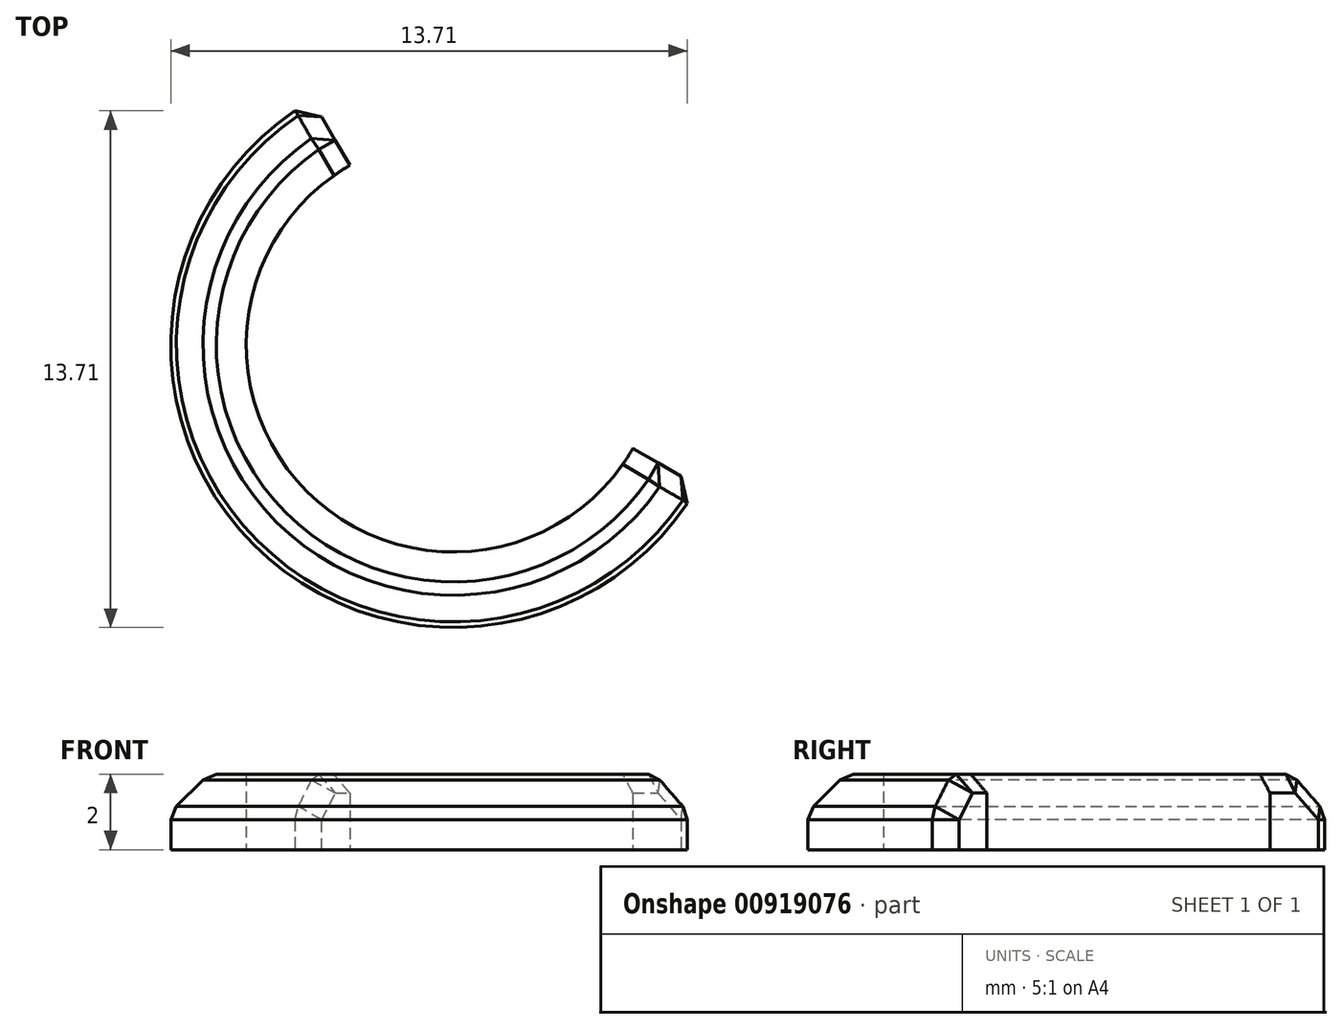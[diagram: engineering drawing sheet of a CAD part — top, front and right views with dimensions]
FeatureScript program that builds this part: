
annotation { "Feature Type Name" : "Feature", "Feature Type Description" : "" }
export const myFeature = defineFeature(function(context is Context, id is Id, definition is map)
    precondition{}
    {
        {
            var Q0;
            Q0=qCreatedBy(makeId("Top.planeOp"),FACE);
            var sketch = newSketch(context, id + "F0", { "sketchPlane" : qUnion([Q0])});
            skCircle(sketch, "E0", {"center": v(0, 0) * mm, "radius": 7.5 * mm});
            skCircle(sketch, "E1", {"center": v(0, 0) * mm, "radius": 5.5 * mm});
            skLineSegment(sketch, "E2", {"start": v(0, 0) * mm, "end": v(-3.75, 6.5) * mm});
            skLineSegment(sketch, "E3", {"start": v(0, 0) * mm, "end": v(6.5, -3.75) * mm});
            skSolve(sketch);
        }
        {
            var Q0;
            {var subQ0=sQuery(id+"F0.wireOp",EDGE,"E2");var subQ1=sQuery(id+"F0.wireOp",EDGE,"E0");var subQ2=makeQuery(id+"F0.imprint","INTERSECT",VERTEX,{"derivedFrom":[subQ1,subQ0]});Q0=makeQuery(id+"F0.imprint","IMPRINT",FACE,{"disambiguationData":[TD([[makeQuery(id+"F0.imprint","IMPRINT",EDGE,{"disambiguationData":[TD([[subQ2,-1.0]])],"derivedFrom":subQ1}),1.0]])]});}
            extrude(context, id + "F1", {"entities" : qUnion([Q0]), "depth" : 2 * mm, "offsetDistance" : 25 * mm});
        }
        {
            var Q0;
            Q0=makeQuery(id+"F1.opExtrude","CAP_EDGE",EDGE,{"disambiguationData":[OSD([sQuery(id+"F0.wireOp",EDGE,"E0")])],"isStart":false});
            chamfer(context, id + "F2", {"entities" : qUnion([Q0]), "width" : 1 * mm, "tangentPropagation" : true});
        }
        {
            var Q0;
            {var subQ0=sQuery(id+"F0.wireOp",EDGE,"E0");Q0=makeQuery(id+"F2.opChamfer","BLEND_EDGE",EDGE,{"blendedFrom":[makeQuery(id+"F1.opExtrude","CAP_EDGE",EDGE,{"disambiguationData":[OSD([subQ0])],"isStart":false}),makeQuery(id+"F1.opExtrude","SWEPT_FACE",FACE,{"disambiguationData":[OSD([subQ0])]})],"blendedInto":[makeQuery(id+"F1.opExtrude","SWEPT_FACE",FACE,{"disambiguationData":[OSD([subQ0])]})]});}
            var Q1;
            {var subQ0=sQuery(id+"F0.wireOp",EDGE,"E0");Q1=makeQuery(id+"F2.opChamfer","BLEND_EDGE",EDGE,{"blendedFrom":[makeQuery(id+"F1.opExtrude","CAP_EDGE",EDGE,{"disambiguationData":[OSD([subQ0])],"isStart":false}),makeQuery(id+"F1.opExtrude","CAP_FACE",FACE,{"disambiguationData":[OSD([subQ0,sQuery(id+"F0.wireOp",EDGE,"E1"),sQuery(id+"F0.wireOp",EDGE,"E2"),sQuery(id+"F0.wireOp",EDGE,"E3")])],"isStart":false})],"blendedInto":[makeQuery(id+"F1.opExtrude","CAP_FACE",FACE,{"disambiguationData":[OSD([subQ0,sQuery(id+"F0.wireOp",EDGE,"E1"),sQuery(id+"F0.wireOp",EDGE,"E2"),sQuery(id+"F0.wireOp",EDGE,"E3")])],"isStart":false})]});}
            var Q2;
            Q2=makeQuery(id+"F1.opExtrude","CAP_EDGE",EDGE,{"disambiguationData":[OSD([sQuery(id+"F0.wireOp",EDGE,"E3")])],"isStart":false});
            var Q3;
            Q3=makeQuery(id+"F2.opChamfer","BLEND_EDGE",EDGE,{"blendedFrom":[makeQuery(id+"F1.opExtrude","CAP_EDGE",EDGE,{"disambiguationData":[OSD([sQuery(id+"F0.wireOp",EDGE,"E0")])],"isStart":false}),makeQuery(id+"F1.opExtrude","SWEPT_FACE",FACE,{"disambiguationData":[OSD([sQuery(id+"F0.wireOp",EDGE,"E3")])]})],"blendedInto":[makeQuery(id+"F1.opExtrude","SWEPT_FACE",FACE,{"disambiguationData":[OSD([sQuery(id+"F0.wireOp",EDGE,"E3")])]})]});
            var Q4;
            Q4=makeQuery(id+"F1.opExtrude","SWEPT_EDGE",EDGE,{"disambiguationData":[OSD([sQuery(id+"F0.wireOp",EDGE,"E0"),sQuery(id+"F0.wireOp",EDGE,"E3")])]});
            var Q5;
            Q5=makeQuery(id+"F1.opExtrude","CAP_EDGE",EDGE,{"disambiguationData":[OSD([sQuery(id+"F0.wireOp",EDGE,"E2")])],"isStart":false});
            var Q6;
            Q6=makeQuery(id+"F2.opChamfer","BLEND_EDGE",EDGE,{"blendedFrom":[makeQuery(id+"F1.opExtrude","CAP_EDGE",EDGE,{"disambiguationData":[OSD([sQuery(id+"F0.wireOp",EDGE,"E0")])],"isStart":false}),makeQuery(id+"F1.opExtrude","SWEPT_FACE",FACE,{"disambiguationData":[OSD([sQuery(id+"F0.wireOp",EDGE,"E2")])]})],"blendedInto":[makeQuery(id+"F1.opExtrude","SWEPT_FACE",FACE,{"disambiguationData":[OSD([sQuery(id+"F0.wireOp",EDGE,"E2")])]})]});
            var Q7;
            Q7=makeQuery(id+"F1.opExtrude","SWEPT_EDGE",EDGE,{"disambiguationData":[OSD([sQuery(id+"F0.wireOp",EDGE,"E0"),sQuery(id+"F0.wireOp",EDGE,"E2")])]});
            chamfer(context, id + "F3", {"entities" : qUnion([Q0, Q1, Q2, Q3, Q4, Q5, Q6, Q7]), "width" : .5 * mm, "tangentPropagation" : true});
        }
    });
